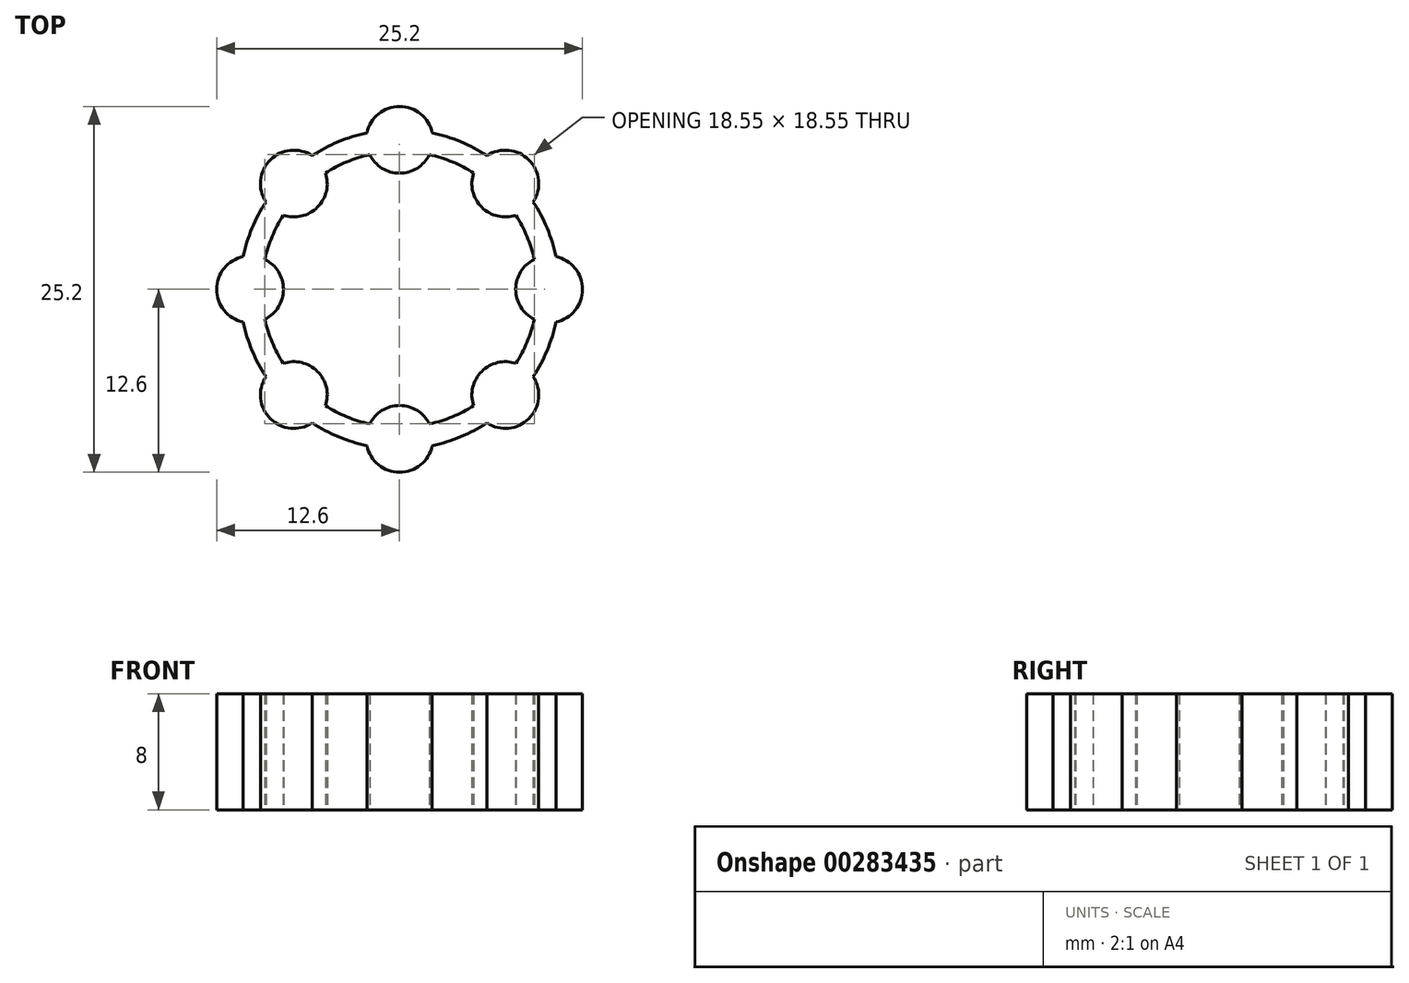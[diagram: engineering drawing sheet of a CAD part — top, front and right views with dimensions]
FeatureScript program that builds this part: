
annotation { "Feature Type Name" : "Feature", "Feature Type Description" : "" }
export const myFeature = defineFeature(function(context is Context, id is Id, definition is map)
    precondition{}
    {
        {
            var Q0;
            Q0=qCreatedBy(makeId("Top.planeOp"),FACE);
            var sketch = newSketch(context, id + "F0", { "sketchPlane" : qUnion([Q0])});
            skCircle(sketch, "E0", {"center": v(0, 0) * mm, "radius": 12.6 * mm});
            skCircle(sketch, "E1", {"center": v(0, 0) * mm, "radius": 8 * mm});
            skCircle(sketch, "E2", {"center": v(0, 0) * mm, "radius": 11 * mm});
            skCircle(sketch, "E3", {"center": v(0, 0) * mm, "radius": 9.5 * mm});
            skCircle(sketch, "E4", {"center": v(0, 10.3) * mm, "radius": 2.3 * mm});
            skCircle(sketch, "E5.1.0", {"center": v(-7.28, 7.28) * mm, "radius": 2.3 * mm});
            skCircle(sketch, "E5.2.0", {"center": v(-10.3, 0) * mm, "radius": 2.3 * mm});
            skCircle(sketch, "E5.3.0", {"center": v(-7.28, -7.28) * mm, "radius": 2.3 * mm});
            skCircle(sketch, "E5.4.0", {"center": v(0, -10.3) * mm, "radius": 2.3 * mm});
            skCircle(sketch, "E5.5.0", {"center": v(7.28, -7.28) * mm, "radius": 2.3 * mm});
            skCircle(sketch, "E5.6.0", {"center": v(10.3, 0) * mm, "radius": 2.3 * mm});
            skCircle(sketch, "E5.7.0", {"center": v(7.28, 7.28) * mm, "radius": 2.3 * mm});
            skSolve(sketch);
        }
        {
            var Q0;
            {var subQ0=sQuery(id+"F0.wireOp",EDGE,"E4");var subQ1=sQuery(id+"F0.wireOp",EDGE,"E2");var subQ2=makeQuery(id+"F0.imprint","INTERSECT",VERTEX,{"disambiguationData":[OD(0.0)],"derivedFrom":[subQ1,subQ0]});Q0=makeQuery(id+"F0.imprint","IMPRINT",FACE,{"disambiguationData":[TD([[makeQuery(id+"F0.imprint","IMPRINT",EDGE,{"disambiguationData":[TD([[subQ2,-1.0]])],"derivedFrom":subQ1}),-1.0]])]});}
            var Q1;
            {var subQ0=sQuery(id+"F0.wireOp",EDGE,"E4");var subQ1=sQuery(id+"F0.wireOp",EDGE,"E2");var subQ2=makeQuery(id+"F0.imprint","INTERSECT",VERTEX,{"disambiguationData":[OD(0.0)],"derivedFrom":[subQ1,subQ0]});Q1=makeQuery(id+"F0.imprint","IMPRINT",FACE,{"disambiguationData":[TD([[makeQuery(id+"F0.imprint","IMPRINT",EDGE,{"disambiguationData":[TD([[subQ2,-1.0]])],"derivedFrom":subQ1}),1.0]])]});}
            var Q2;
            {var subQ0=sQuery(id+"F0.wireOp",EDGE,"E4");var subQ1=sQuery(id+"F0.wireOp",EDGE,"E3");var subQ2=makeQuery(id+"F0.imprint","INTERSECT",VERTEX,{"disambiguationData":[OD(0.0)],"derivedFrom":[subQ1,subQ0]});Q2=makeQuery(id+"F0.imprint","IMPRINT",FACE,{"disambiguationData":[TD([[makeQuery(id+"F0.imprint","IMPRINT",EDGE,{"disambiguationData":[TD([[subQ2,-1.0]])],"derivedFrom":subQ1}),1.0]])]});}
            var Q3;
            {var subQ0=sQuery(id+"F0.wireOp",EDGE,"E4");var subQ1=sQuery(id+"F0.wireOp",EDGE,"E2");var subQ2=makeQuery(id+"F0.imprint","INTERSECT",VERTEX,{"disambiguationData":[OD(1.0)],"derivedFrom":[subQ1,subQ0]});Q3=makeQuery(id+"F0.imprint","IMPRINT",FACE,{"disambiguationData":[TD([[makeQuery(id+"F0.imprint","IMPRINT",EDGE,{"disambiguationData":[TD([[subQ2,-1.0]])],"derivedFrom":subQ1}),1.0]])]});}
            var Q4;
            {var subQ0=sQuery(id+"F0.wireOp",EDGE,"E5.1.0");var subQ1=sQuery(id+"F0.wireOp",EDGE,"E2");var subQ2=makeQuery(id+"F0.imprint","INTERSECT",VERTEX,{"disambiguationData":[OD(0.0)],"derivedFrom":[subQ1,subQ0]});Q4=makeQuery(id+"F0.imprint","IMPRINT",FACE,{"disambiguationData":[TD([[makeQuery(id+"F0.imprint","IMPRINT",EDGE,{"disambiguationData":[TD([[subQ2,-1.0]])],"derivedFrom":subQ1}),-1.0]])]});}
            var Q5;
            {var subQ0=sQuery(id+"F0.wireOp",EDGE,"E5.1.0");var subQ1=sQuery(id+"F0.wireOp",EDGE,"E2");var subQ2=makeQuery(id+"F0.imprint","INTERSECT",VERTEX,{"disambiguationData":[OD(0.0)],"derivedFrom":[subQ1,subQ0]});Q5=makeQuery(id+"F0.imprint","IMPRINT",FACE,{"disambiguationData":[TD([[makeQuery(id+"F0.imprint","IMPRINT",EDGE,{"disambiguationData":[TD([[subQ2,-1.0]])],"derivedFrom":subQ1}),1.0]])]});}
            var Q6;
            {var subQ0=sQuery(id+"F0.wireOp",EDGE,"E5.1.0");var subQ1=sQuery(id+"F0.wireOp",EDGE,"E3");var subQ2=makeQuery(id+"F0.imprint","INTERSECT",VERTEX,{"disambiguationData":[OD(0.0)],"derivedFrom":[subQ1,subQ0]});Q6=makeQuery(id+"F0.imprint","IMPRINT",FACE,{"disambiguationData":[TD([[makeQuery(id+"F0.imprint","IMPRINT",EDGE,{"disambiguationData":[TD([[subQ2,-1.0]])],"derivedFrom":subQ1}),1.0]])]});}
            var Q7;
            {var subQ0=sQuery(id+"F0.wireOp",EDGE,"E5.1.0");var subQ1=sQuery(id+"F0.wireOp",EDGE,"E2");var subQ2=makeQuery(id+"F0.imprint","INTERSECT",VERTEX,{"disambiguationData":[OD(1.0)],"derivedFrom":[subQ1,subQ0]});Q7=makeQuery(id+"F0.imprint","IMPRINT",FACE,{"disambiguationData":[TD([[makeQuery(id+"F0.imprint","IMPRINT",EDGE,{"disambiguationData":[TD([[subQ2,-1.0]])],"derivedFrom":subQ1}),1.0]])]});}
            var Q8;
            {var subQ0=sQuery(id+"F0.wireOp",EDGE,"E5.2.0");var subQ1=sQuery(id+"F0.wireOp",EDGE,"E2");var subQ2=makeQuery(id+"F0.imprint","INTERSECT",VERTEX,{"disambiguationData":[OD(0.0)],"derivedFrom":[subQ1,subQ0]});Q8=makeQuery(id+"F0.imprint","IMPRINT",FACE,{"disambiguationData":[TD([[makeQuery(id+"F0.imprint","IMPRINT",EDGE,{"disambiguationData":[TD([[subQ2,-1.0]])],"derivedFrom":subQ1}),-1.0]])]});}
            var Q9;
            {var subQ0=sQuery(id+"F0.wireOp",EDGE,"E5.2.0");var subQ1=sQuery(id+"F0.wireOp",EDGE,"E2");var subQ2=makeQuery(id+"F0.imprint","INTERSECT",VERTEX,{"disambiguationData":[OD(0.0)],"derivedFrom":[subQ1,subQ0]});Q9=makeQuery(id+"F0.imprint","IMPRINT",FACE,{"disambiguationData":[TD([[makeQuery(id+"F0.imprint","IMPRINT",EDGE,{"disambiguationData":[TD([[subQ2,-1.0]])],"derivedFrom":subQ1}),1.0]])]});}
            var Q10;
            {var subQ0=sQuery(id+"F0.wireOp",EDGE,"E5.2.0");var subQ1=sQuery(id+"F0.wireOp",EDGE,"E3");var subQ2=makeQuery(id+"F0.imprint","INTERSECT",VERTEX,{"disambiguationData":[OD(0.0)],"derivedFrom":[subQ1,subQ0]});Q10=makeQuery(id+"F0.imprint","IMPRINT",FACE,{"disambiguationData":[TD([[makeQuery(id+"F0.imprint","IMPRINT",EDGE,{"disambiguationData":[TD([[subQ2,-1.0]])],"derivedFrom":subQ1}),1.0]])]});}
            var Q11;
            {var subQ0=sQuery(id+"F0.wireOp",EDGE,"E5.2.0");var subQ1=sQuery(id+"F0.wireOp",EDGE,"E2");var subQ2=makeQuery(id+"F0.imprint","INTERSECT",VERTEX,{"disambiguationData":[OD(1.0)],"derivedFrom":[subQ1,subQ0]});Q11=makeQuery(id+"F0.imprint","IMPRINT",FACE,{"disambiguationData":[TD([[makeQuery(id+"F0.imprint","IMPRINT",EDGE,{"disambiguationData":[TD([[subQ2,-1.0]])],"derivedFrom":subQ1}),1.0]])]});}
            var Q12;
            {var subQ0=sQuery(id+"F0.wireOp",EDGE,"E5.3.0");var subQ1=sQuery(id+"F0.wireOp",EDGE,"E2");var subQ2=makeQuery(id+"F0.imprint","INTERSECT",VERTEX,{"disambiguationData":[OD(0.0)],"derivedFrom":[subQ1,subQ0]});Q12=makeQuery(id+"F0.imprint","IMPRINT",FACE,{"disambiguationData":[TD([[makeQuery(id+"F0.imprint","IMPRINT",EDGE,{"disambiguationData":[TD([[subQ2,-1.0]])],"derivedFrom":subQ1}),-1.0]])]});}
            var Q13;
            {var subQ0=sQuery(id+"F0.wireOp",EDGE,"E5.3.0");var subQ1=sQuery(id+"F0.wireOp",EDGE,"E2");var subQ2=makeQuery(id+"F0.imprint","INTERSECT",VERTEX,{"disambiguationData":[OD(0.0)],"derivedFrom":[subQ1,subQ0]});Q13=makeQuery(id+"F0.imprint","IMPRINT",FACE,{"disambiguationData":[TD([[makeQuery(id+"F0.imprint","IMPRINT",EDGE,{"disambiguationData":[TD([[subQ2,-1.0]])],"derivedFrom":subQ1}),1.0]])]});}
            var Q14;
            {var subQ0=sQuery(id+"F0.wireOp",EDGE,"E5.3.0");var subQ1=sQuery(id+"F0.wireOp",EDGE,"E3");var subQ2=makeQuery(id+"F0.imprint","INTERSECT",VERTEX,{"disambiguationData":[OD(0.0)],"derivedFrom":[subQ1,subQ0]});Q14=makeQuery(id+"F0.imprint","IMPRINT",FACE,{"disambiguationData":[TD([[makeQuery(id+"F0.imprint","IMPRINT",EDGE,{"disambiguationData":[TD([[subQ2,-1.0]])],"derivedFrom":subQ1}),1.0]])]});}
            var Q15;
            {var subQ0=sQuery(id+"F0.wireOp",EDGE,"E5.3.0");var subQ1=sQuery(id+"F0.wireOp",EDGE,"E2");var subQ2=makeQuery(id+"F0.imprint","INTERSECT",VERTEX,{"disambiguationData":[OD(1.0)],"derivedFrom":[subQ1,subQ0]});Q15=makeQuery(id+"F0.imprint","IMPRINT",FACE,{"disambiguationData":[TD([[makeQuery(id+"F0.imprint","IMPRINT",EDGE,{"disambiguationData":[TD([[subQ2,-1.0]])],"derivedFrom":subQ1}),1.0]])]});}
            var Q16;
            {var subQ0=sQuery(id+"F0.wireOp",EDGE,"E5.4.0");var subQ1=sQuery(id+"F0.wireOp",EDGE,"E3");var subQ2=makeQuery(id+"F0.imprint","INTERSECT",VERTEX,{"disambiguationData":[OD(0.0)],"derivedFrom":[subQ1,subQ0]});Q16=makeQuery(id+"F0.imprint","IMPRINT",FACE,{"disambiguationData":[TD([[makeQuery(id+"F0.imprint","IMPRINT",EDGE,{"disambiguationData":[TD([[subQ2,-1.0]])],"derivedFrom":subQ1}),1.0]])]});}
            var Q17;
            {var subQ0=sQuery(id+"F0.wireOp",EDGE,"E5.4.0");var subQ1=sQuery(id+"F0.wireOp",EDGE,"E2");var subQ2=makeQuery(id+"F0.imprint","INTERSECT",VERTEX,{"disambiguationData":[OD(0.0)],"derivedFrom":[subQ1,subQ0]});Q17=makeQuery(id+"F0.imprint","IMPRINT",FACE,{"disambiguationData":[TD([[makeQuery(id+"F0.imprint","IMPRINT",EDGE,{"disambiguationData":[TD([[subQ2,-1.0]])],"derivedFrom":subQ1}),1.0]])]});}
            var Q18;
            {var subQ0=sQuery(id+"F0.wireOp",EDGE,"E5.4.0");var subQ1=sQuery(id+"F0.wireOp",EDGE,"E2");var subQ2=makeQuery(id+"F0.imprint","INTERSECT",VERTEX,{"disambiguationData":[OD(0.0)],"derivedFrom":[subQ1,subQ0]});Q18=makeQuery(id+"F0.imprint","IMPRINT",FACE,{"disambiguationData":[TD([[makeQuery(id+"F0.imprint","IMPRINT",EDGE,{"disambiguationData":[TD([[subQ2,-1.0]])],"derivedFrom":subQ1}),-1.0]])]});}
            var Q19;
            {var subQ0=sQuery(id+"F0.wireOp",EDGE,"E5.4.0");var subQ1=sQuery(id+"F0.wireOp",EDGE,"E2");var subQ2=makeQuery(id+"F0.imprint","INTERSECT",VERTEX,{"disambiguationData":[OD(1.0)],"derivedFrom":[subQ1,subQ0]});Q19=makeQuery(id+"F0.imprint","IMPRINT",FACE,{"disambiguationData":[TD([[makeQuery(id+"F0.imprint","IMPRINT",EDGE,{"disambiguationData":[TD([[subQ2,-1.0]])],"derivedFrom":subQ1}),1.0]])]});}
            var Q20;
            {var subQ0=sQuery(id+"F0.wireOp",EDGE,"E5.5.0");var subQ1=sQuery(id+"F0.wireOp",EDGE,"E3");var subQ2=makeQuery(id+"F0.imprint","INTERSECT",VERTEX,{"disambiguationData":[OD(0.0)],"derivedFrom":[subQ1,subQ0]});Q20=makeQuery(id+"F0.imprint","IMPRINT",FACE,{"disambiguationData":[TD([[makeQuery(id+"F0.imprint","IMPRINT",EDGE,{"disambiguationData":[TD([[subQ2,-1.0]])],"derivedFrom":subQ1}),1.0]])]});}
            var Q21;
            {var subQ0=sQuery(id+"F0.wireOp",EDGE,"E5.5.0");var subQ1=sQuery(id+"F0.wireOp",EDGE,"E2");var subQ2=makeQuery(id+"F0.imprint","INTERSECT",VERTEX,{"disambiguationData":[OD(0.0)],"derivedFrom":[subQ1,subQ0]});Q21=makeQuery(id+"F0.imprint","IMPRINT",FACE,{"disambiguationData":[TD([[makeQuery(id+"F0.imprint","IMPRINT",EDGE,{"disambiguationData":[TD([[subQ2,-1.0]])],"derivedFrom":subQ1}),1.0]])]});}
            var Q22;
            {var subQ0=sQuery(id+"F0.wireOp",EDGE,"E5.5.0");var subQ1=sQuery(id+"F0.wireOp",EDGE,"E2");var subQ2=makeQuery(id+"F0.imprint","INTERSECT",VERTEX,{"disambiguationData":[OD(0.0)],"derivedFrom":[subQ1,subQ0]});Q22=makeQuery(id+"F0.imprint","IMPRINT",FACE,{"disambiguationData":[TD([[makeQuery(id+"F0.imprint","IMPRINT",EDGE,{"disambiguationData":[TD([[subQ2,-1.0]])],"derivedFrom":subQ1}),-1.0]])]});}
            var Q23;
            {var subQ0=sQuery(id+"F0.wireOp",EDGE,"E5.5.0");var subQ1=sQuery(id+"F0.wireOp",EDGE,"E2");var subQ2=makeQuery(id+"F0.imprint","INTERSECT",VERTEX,{"disambiguationData":[OD(1.0)],"derivedFrom":[subQ1,subQ0]});Q23=makeQuery(id+"F0.imprint","IMPRINT",FACE,{"disambiguationData":[TD([[makeQuery(id+"F0.imprint","IMPRINT",EDGE,{"disambiguationData":[TD([[subQ2,-1.0]])],"derivedFrom":subQ1}),1.0]])]});}
            var Q24;
            {var subQ0=sQuery(id+"F0.wireOp",EDGE,"E5.6.0");var subQ1=sQuery(id+"F0.wireOp",EDGE,"E2");var subQ2=makeQuery(id+"F0.imprint","INTERSECT",VERTEX,{"disambiguationData":[OD(0.0)],"derivedFrom":[subQ1,subQ0]});Q24=makeQuery(id+"F0.imprint","IMPRINT",FACE,{"disambiguationData":[TD([[makeQuery(id+"F0.imprint","IMPRINT",EDGE,{"disambiguationData":[TD([[subQ2,1.0]])],"derivedFrom":subQ1}),-1.0]])]});}
            var Q25;
            {var subQ0=sQuery(id+"F0.wireOp",EDGE,"E5.6.0");var subQ1=sQuery(id+"F0.wireOp",EDGE,"E2");var subQ2=makeQuery(id+"F0.imprint","INTERSECT",VERTEX,{"disambiguationData":[OD(0.0)],"derivedFrom":[subQ1,subQ0]});Q25=makeQuery(id+"F0.imprint","IMPRINT",FACE,{"disambiguationData":[TD([[makeQuery(id+"F0.imprint","IMPRINT",EDGE,{"disambiguationData":[TD([[subQ2,1.0]])],"derivedFrom":subQ1}),1.0]])]});}
            var Q26;
            {var subQ0=sQuery(id+"F0.wireOp",EDGE,"E5.6.0");var subQ1=sQuery(id+"F0.wireOp",EDGE,"E3");var subQ2=makeQuery(id+"F0.imprint","INTERSECT",VERTEX,{"disambiguationData":[OD(0.0)],"derivedFrom":[subQ1,subQ0]});Q26=makeQuery(id+"F0.imprint","IMPRINT",FACE,{"disambiguationData":[TD([[makeQuery(id+"F0.imprint","IMPRINT",EDGE,{"disambiguationData":[TD([[subQ2,1.0]])],"derivedFrom":subQ1}),1.0]])]});}
            var Q27;
            {var subQ0=sQuery(id+"F0.wireOp",EDGE,"E5.7.0");var subQ1=sQuery(id+"F0.wireOp",EDGE,"E2");var subQ2=makeQuery(id+"F0.imprint","INTERSECT",VERTEX,{"disambiguationData":[OD(0.0)],"derivedFrom":[subQ1,subQ0]});Q27=makeQuery(id+"F0.imprint","IMPRINT",FACE,{"disambiguationData":[TD([[makeQuery(id+"F0.imprint","IMPRINT",EDGE,{"disambiguationData":[TD([[subQ2,1.0]])],"derivedFrom":subQ1}),1.0]])]});}
            var Q28;
            {var subQ0=sQuery(id+"F0.wireOp",EDGE,"E5.7.0");var subQ1=sQuery(id+"F0.wireOp",EDGE,"E2");var subQ2=makeQuery(id+"F0.imprint","INTERSECT",VERTEX,{"disambiguationData":[OD(0.0)],"derivedFrom":[subQ1,subQ0]});Q28=makeQuery(id+"F0.imprint","IMPRINT",FACE,{"disambiguationData":[TD([[makeQuery(id+"F0.imprint","IMPRINT",EDGE,{"disambiguationData":[TD([[subQ2,-1.0]])],"derivedFrom":subQ1}),-1.0]])]});}
            var Q29;
            {var subQ0=sQuery(id+"F0.wireOp",EDGE,"E5.7.0");var subQ1=sQuery(id+"F0.wireOp",EDGE,"E2");var subQ2=makeQuery(id+"F0.imprint","INTERSECT",VERTEX,{"disambiguationData":[OD(0.0)],"derivedFrom":[subQ1,subQ0]});Q29=makeQuery(id+"F0.imprint","IMPRINT",FACE,{"disambiguationData":[TD([[makeQuery(id+"F0.imprint","IMPRINT",EDGE,{"disambiguationData":[TD([[subQ2,-1.0]])],"derivedFrom":subQ1}),1.0]])]});}
            var Q30;
            {var subQ0=sQuery(id+"F0.wireOp",EDGE,"E5.7.0");var subQ1=sQuery(id+"F0.wireOp",EDGE,"E3");var subQ2=makeQuery(id+"F0.imprint","INTERSECT",VERTEX,{"disambiguationData":[OD(0.0)],"derivedFrom":[subQ1,subQ0]});Q30=makeQuery(id+"F0.imprint","IMPRINT",FACE,{"disambiguationData":[TD([[makeQuery(id+"F0.imprint","IMPRINT",EDGE,{"disambiguationData":[TD([[subQ2,-1.0]])],"derivedFrom":subQ1}),1.0]])]});}
            var Q31;
            {var subQ0=sQuery(id+"F0.wireOp",EDGE,"E5.7.0");var subQ1=sQuery(id+"F0.wireOp",EDGE,"E2");var subQ2=makeQuery(id+"F0.imprint","INTERSECT",VERTEX,{"disambiguationData":[OD(1.0)],"derivedFrom":[subQ1,subQ0]});Q31=makeQuery(id+"F0.imprint","IMPRINT",FACE,{"disambiguationData":[TD([[makeQuery(id+"F0.imprint","IMPRINT",EDGE,{"disambiguationData":[TD([[subQ2,-1.0]])],"derivedFrom":subQ1}),1.0]])]});}
            extrude(context, id + "F1", {"entities" : qUnion([Q0, Q1, Q2, Q3, Q4, Q5, Q6, Q7, Q8, Q9, Q10, Q11, Q12, Q13, Q14, Q15, Q16, Q17, Q18, Q19, Q20, Q21, Q22, Q23, Q24, Q25, Q26, Q27, Q28, Q29, Q30, Q31]), "depth" : 8 * mm, "offsetDistance" : 25 * mm});
        }
    });
